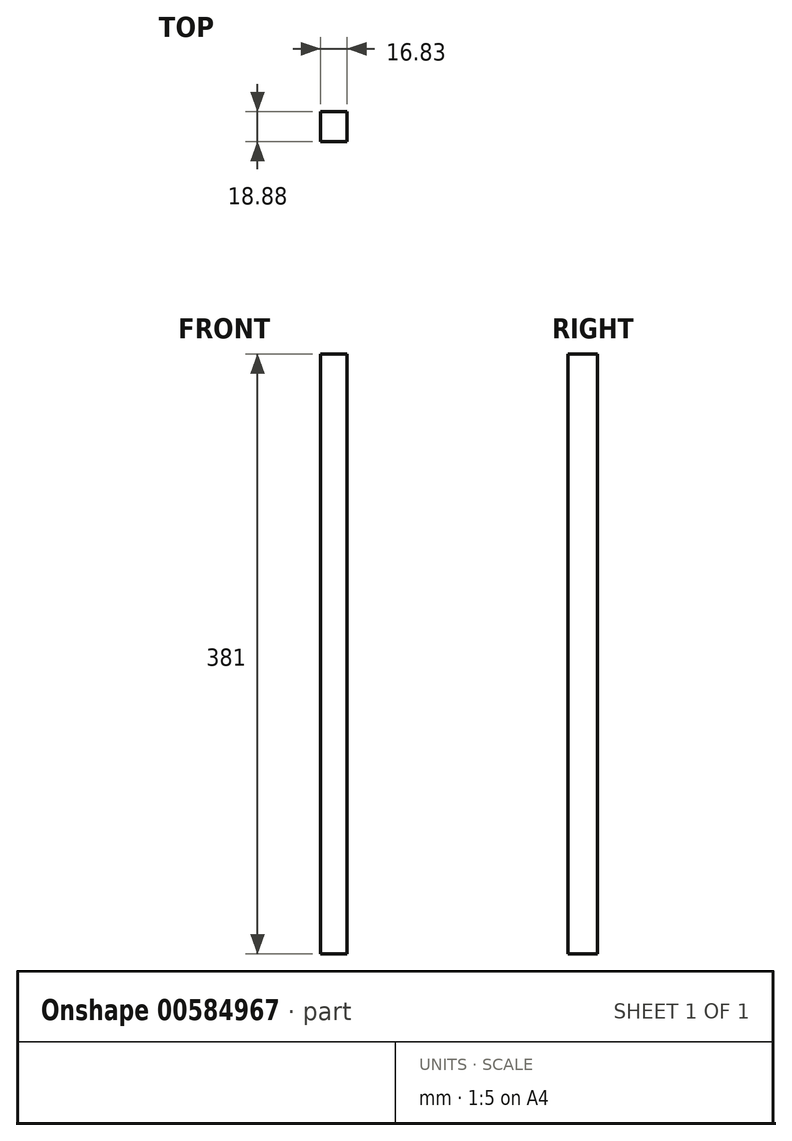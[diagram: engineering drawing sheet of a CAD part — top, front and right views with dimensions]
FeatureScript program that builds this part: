
annotation { "Feature Type Name" : "Feature", "Feature Type Description" : "" }
export const myFeature = defineFeature(function(context is Context, id is Id, definition is map)
    precondition{}
    {
        {
            var Q0;
            Q0=qCreatedBy(makeId("Top.planeOp"),FACE);
            var sketch = newSketch(context, id + "F0", { "sketchPlane" : qUnion([Q0])});
            skLineSegment(sketch, "E0.bottom", {"start": v(-7.04, 8.41) * mm, "end": v(9.79, 8.41) * mm});
            skLineSegment(sketch, "E0.top", {"start": v(-7.04, -10.47) * mm, "end": v(9.79, -10.47) * mm});
            skLineSegment(sketch, "E0.left", {"start": v(-7.04, 8.41) * mm, "end": v(-7.04, -10.47) * mm});
            skLineSegment(sketch, "E0.right", {"start": v(9.79, 8.41) * mm, "end": v(9.79, -10.47) * mm});
            skSolve(sketch);
        }
        {
            var Q0;
            Q0=makeQuery(id+"F0.imprint","IMPRINT",FACE,{"disambiguationData":[TD([[makeQuery(id+"F0.imprint","IMPRINT",EDGE,{"derivedFrom":sQuery(id+"F0.wireOp",EDGE,"E0.bottom")}),-1.0]])]});
            extrude(context, id + "F1", {"entities" : qUnion([Q0]), "depth" : 381 * mm, "offsetDistance" : 25.4 * mm});
        }
    });
